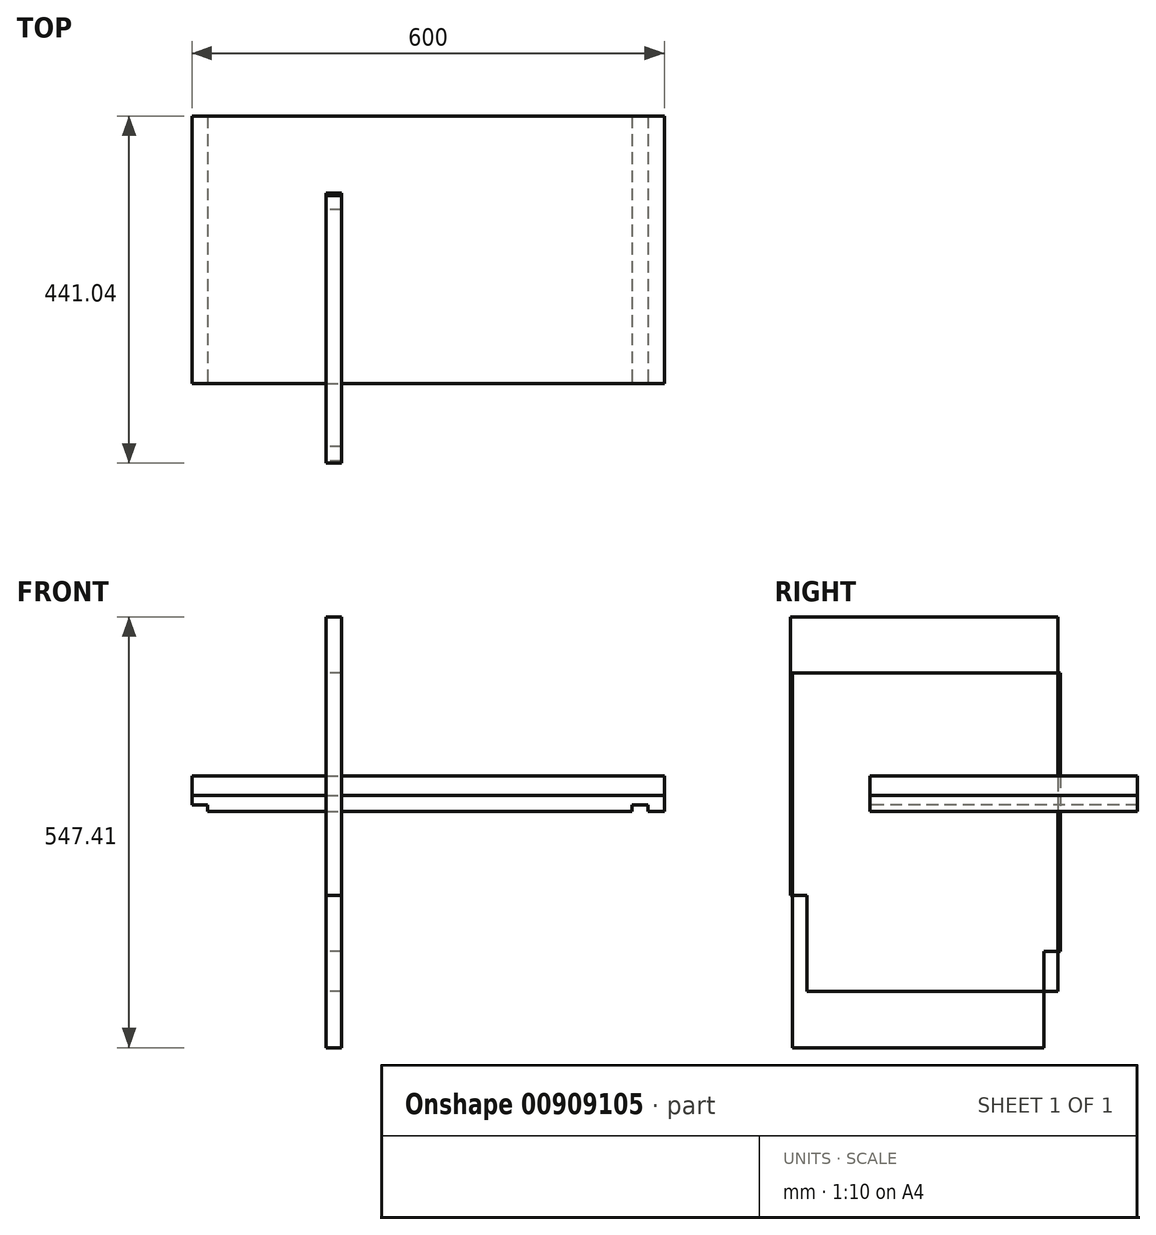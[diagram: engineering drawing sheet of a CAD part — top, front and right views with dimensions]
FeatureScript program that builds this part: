
annotation { "Feature Type Name" : "Feature", "Feature Type Description" : "" }
export const myFeature = defineFeature(function(context is Context, id is Id, definition is map)
    precondition{}
    {
        {
            assignVariable(context, id + "F0", {"name" : "Thick_major", "anyValue" : 20});
        }
        {
            assignVariable(context, id + "F1", {"name" : "Rebate", "anyValue" : 8});
        }
        {
            var Q0;
            Q0=qCreatedBy(makeId("Top.planeOp"),FACE);
            var sketch = newSketch(context, id + "F2", { "sketchPlane" : qUnion([Q0])});
            skLineSegment(sketch, "E0.bottom", {"start": v(-170.28, 270.48) * mm, "end": v(429.72, 270.48) * mm});
            skLineSegment(sketch, "E0.top", {"start": v(-170.28, -69.52) * mm, "end": v(429.72, -69.52) * mm});
            skLineSegment(sketch, "E0.left", {"start": v(-170.28, 270.48) * mm, "end": v(-170.28, -69.52) * mm});
            skLineSegment(sketch, "E0.right", {"start": v(429.72, 270.48) * mm, "end": v(429.72, -69.52) * mm});
            skLineSegment(sketch, "E1.bottom", {"start": v(-170.28, 270.48) * mm, "end": v(-150.28, 270.48) * mm});
            skLineSegment(sketch, "E1.top", {"start": v(-170.28, -69.52) * mm, "end": v(-150.28, -69.52) * mm});
            skLineSegment(sketch, "E1.right", {"start": v(-150.28, 270.48) * mm, "end": v(-150.28, -69.52) * mm});
            skLineSegment(sketch, "E2.bottom", {"start": v(388.72, 270.48) * mm, "end": v(408.72, 270.48) * mm});
            skLineSegment(sketch, "E2.top", {"start": v(388.72, -69.52) * mm, "end": v(408.72, -69.52) * mm});
            skLineSegment(sketch, "E2.left", {"start": v(388.72, 270.48) * mm, "end": v(388.72, -69.52) * mm});
            skLineSegment(sketch, "E2.right", {"start": v(408.72, 270.48) * mm, "end": v(408.72, -69.52) * mm});
            skSolve(sketch);
        }
        {
            var Q0;
            {var subQ2=sQuery(id+"F2.wireOp",EDGE,"E0.left");Q0=makeQuery(id+"F2.imprint","IMPRINT",FACE,{"disambiguationData":[TD([[makeQuery(id+"F2.imprint","IMPRINT",EDGE,{"derivedFrom":subQ2}),1.0]])]});}
            var Q1;
            {var subQ0=sQuery(id+"F2.wireOp",EDGE,"E1.right");Q1=makeQuery(id+"F2.imprint","IMPRINT",FACE,{"disambiguationData":[TD([[makeQuery(id+"F2.imprint","IMPRINT",EDGE,{"derivedFrom":subQ0}),1.0]])]});}
            var Q2;
            {var subQ0=sQuery(id+"F2.wireOp",EDGE,"E2.left");Q2=makeQuery(id+"F2.imprint","IMPRINT",FACE,{"disambiguationData":[TD([[makeQuery(id+"F2.imprint","IMPRINT",EDGE,{"derivedFrom":subQ0}),1.0]])]});}
            var Q3;
            {var subQ0=sQuery(id+"F2.wireOp",EDGE,"E0.right");Q3=makeQuery(id+"F2.imprint","IMPRINT",FACE,{"disambiguationData":[TD([[makeQuery(id+"F2.imprint","IMPRINT",EDGE,{"derivedFrom":subQ0}),-1.0]])]});}
            extrude(context, id + "F3", {"entities" : qUnion([Q0, Q1, Q2, Q3]), "oppositeDirection" : true, "depth" : getVariable(context, 'Thick_major') * mm, "offsetDistance" : 25 * mm});
        }
        {
            var Q0;
            {var subQ2=sQuery(id+"F2.wireOp",EDGE,"E0.left");Q0=makeQuery(id+"F2.imprint","IMPRINT",FACE,{"disambiguationData":[TD([[makeQuery(id+"F2.imprint","IMPRINT",EDGE,{"derivedFrom":subQ2}),1.0]])]});}
            var Q1;
            {var subQ0=sQuery(id+"F2.wireOp",EDGE,"E2.left");Q1=makeQuery(id+"F2.imprint","IMPRINT",FACE,{"disambiguationData":[TD([[makeQuery(id+"F2.imprint","IMPRINT",EDGE,{"derivedFrom":subQ0}),1.0]])]});}
            extrude(context, id + "F4", {"entities" : qUnion([Q0, Q1]), "operationType" : NewBodyOperationType.REMOVE, "oppositeDirection" : true, "depth" : (getVariable(context, 'Thick_major')) * mm, "offsetDistance" : 25 * mm, "hasSecondDirection" : true, "secondDirectionOppositeDirection" : true, "secondDirectionDepth" : (getVariable(context, 'Thick_major') - getVariable(context, 'Rebate')) * mm});
        }
        {
            var Q0;
            Q0=qCreatedBy(makeId("Right.planeOp"),FACE);
            var sketch = newSketch(context, id + "F5", { "sketchPlane" : qUnion([Q0])});
            skLineSegment(sketch, "E3.bottom", {"start": v(172.43, 155.8) * mm, "end": v(-167.57, 155.8) * mm});
            skLineSegment(sketch, "E3.top", {"start": v(172.43, -320.2) * mm, "end": v(-167.57, -320.2) * mm});
            skLineSegment(sketch, "E3.left", {"start": v(172.43, 155.8) * mm, "end": v(172.43, -320.2) * mm});
            skLineSegment(sketch, "E3.right", {"start": v(-167.57, 155.8) * mm, "end": v(-167.57, -320.2) * mm});
            skLineSegment(sketch, "E4.top", {"start": v(-167.57, -320.2) * mm, "end": v(-146.57, -320.2) * mm});
            skLineSegment(sketch, "E4.left", {"start": v(-167.57, -198.2) * mm, "end": v(-167.57, -320.2) * mm});
            skLineSegment(sketch, "E5.bottom", {"start": v(172.43, -198.2) * mm, "end": v(151.43, -198.2) * mm});
            skLineSegment(sketch, "E5.top", {"start": v(172.43, -320.2) * mm, "end": v(151.43, -320.2) * mm});
            skLineSegment(sketch, "E5.left", {"start": v(172.43, -198.2) * mm, "end": v(172.43, -320.2) * mm});
            skLineSegment(sketch, "E5.right", {"start": v(151.43, -198.2) * mm, "end": v(151.43, -320.2) * mm});
            skSolve(sketch);
        }
        {
            var Q0;
            Q0=makeQuery(id+"F5.imprint","IMPRINT",FACE,{"disambiguationData":[TD([[makeQuery(id+"F5.imprint","IMPRINT",EDGE,{"derivedFrom":sQuery(id+"F5.wireOp",EDGE,"E3.bottom")}),1.0]])]});
            extrude(context, id + "F6", {"entities" : qUnion([Q0]), "depth" : (getVariable(context, 'Thick_major')) * mm, "offsetDistance" : 25 * mm});
        }
        {
            var Q0;
            Q0=qCreatedBy(makeId("Right.planeOp"),FACE);
            var sketch = newSketch(context, id + "F7", { "sketchPlane" : qUnion([Q0])});
            skLineSegment(sketch, "E6.bottom", {"start": v(-170.56, 227.2) * mm, "end": v(169.44, 227.2) * mm});
            skLineSegment(sketch, "E6.top", {"start": v(-170.56, -248.8) * mm, "end": v(169.44, -248.8) * mm});
            skLineSegment(sketch, "E6.left", {"start": v(-170.56, 227.2) * mm, "end": v(-170.56, -248.8) * mm});
            skLineSegment(sketch, "E6.right", {"start": v(169.44, 227.2) * mm, "end": v(169.44, -248.8) * mm});
            skLineSegment(sketch, "E7.bottom", {"start": v(-170.56, -126.8) * mm, "end": v(-149.56, -126.8) * mm});
            skLineSegment(sketch, "E7.top", {"start": v(-170.56, -248.8) * mm, "end": v(-149.56, -248.8) * mm});
            skLineSegment(sketch, "E7.left", {"start": v(-170.56, -126.8) * mm, "end": v(-170.56, -248.8) * mm});
            skLineSegment(sketch, "E7.right", {"start": v(-149.56, -126.8) * mm, "end": v(-149.56, -248.8) * mm});
            skSolve(sketch);
        }
        {
            var Q0;
            {var subQ1=sQuery(id+"F7.wireOp",EDGE,"E6.bottom");Q0=makeQuery(id+"F7.imprint","IMPRINT",FACE,{"disambiguationData":[TD([[makeQuery(id+"F7.imprint","IMPRINT",EDGE,{"derivedFrom":subQ1}),-1.0]])]});}
            extrude(context, id + "F8", {"entities" : qUnion([Q0]), "depth" : (getVariable(context, 'Thick_major')) * mm, "offsetDistance" : 25 * mm});
        }
        {
            var Q0;
            {var subQ2=sQuery(id+"F2.wireOp",EDGE,"E0.left");Q0=makeQuery(id+"F2.imprint","IMPRINT",FACE,{"disambiguationData":[TD([[makeQuery(id+"F2.imprint","IMPRINT",EDGE,{"derivedFrom":subQ2}),1.0]])]});}
            var Q1;
            {var subQ0=sQuery(id+"F2.wireOp",EDGE,"E1.right");Q1=makeQuery(id+"F2.imprint","IMPRINT",FACE,{"disambiguationData":[TD([[makeQuery(id+"F2.imprint","IMPRINT",EDGE,{"derivedFrom":subQ0}),1.0]])]});}
            var Q2;
            {var subQ0=sQuery(id+"F2.wireOp",EDGE,"E2.left");Q2=makeQuery(id+"F2.imprint","IMPRINT",FACE,{"disambiguationData":[TD([[makeQuery(id+"F2.imprint","IMPRINT",EDGE,{"derivedFrom":subQ0}),1.0]])]});}
            var Q3;
            {var subQ0=sQuery(id+"F2.wireOp",EDGE,"E0.right");Q3=makeQuery(id+"F2.imprint","IMPRINT",FACE,{"disambiguationData":[TD([[makeQuery(id+"F2.imprint","IMPRINT",EDGE,{"derivedFrom":subQ0}),-1.0]])]});}
            extrude(context, id + "F9", {"entities" : qUnion([Q0, Q1, Q2, Q3]), "depth" : 25 * mm, "offsetDistance" : 25 * mm});
        }
    });
